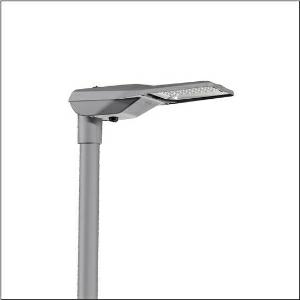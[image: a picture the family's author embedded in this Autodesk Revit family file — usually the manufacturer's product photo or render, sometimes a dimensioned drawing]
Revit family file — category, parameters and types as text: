
# Revit family: streetlight_sl_21_mini___p0_5a_5xe2v33t08gb_dcd0
name_source: partatom
category: Lighting Fixtures
units: mm (PartAtom-declared; Revit-internal decimal feet)

## family parameters
Cut with Voids When Loaded = No
Host = Face
Light Source = No
Part Type = Normal
Room Calculation Point = No
Round Connector Dimension = Use Diameter
Shared = No

## types (1)
- --- (1 x LED, 5840 lm, 40.4 W, 3000K)
    Apparent Load = 40 VA
    CIE Flux Codes = 37 73 96 100 100
    Color Rendering = 70
    Color Temperature = 3000K
    Default Elevation = 1800 mm
    Description = Streetlight SL 21 mini, mast luminaire, primary light control with lens, of PMMA, primary optical cover: cover, of toughened safety glass, transparent, light distribution: P0.5a, light emission: direct distribution, primary light characteristic: asymmetric, installation type: post-top, side-entry, LED, High Power LED, rated luminous flux: 5.840lm, luminous efficacy: 145lm/W, light colour: 730, colour temperature: 3000K, control gear: D4i, control: pre-setting: logarithmic dimming characteristic, flexible luminous flux parameterisation, time-dependent luminous flux control, constant luminous flux control, overheat protection, mains connection: 220..240V, AC, 50/60Hz, start of lifetime: 40W, end of service life: 41W, reduction: 19W, luminaire housing, of diecast aluminium, powder-coated, SITECO metallic grey (DB 702S), corrosivity category C5 high according to DIN EN ISO 12944, multi-level sealing system, sealing non-destructively replaceable, inclination adjustable: 0°, 5°, 10°, 15°, please order mast flange separately, length: 628mm, width: 235mm, height: 110mm, mast flange for spigot size: 42mm (side-entry): 5XC10008XM4, 60/48mm (side-entry/post-top): 5XC10108XM2, 76/60mm (side-entry/post-top): 5XC10108XM1, mounting height: 4..8m, Smart Interface below and above, protection rating (complete): IP66, insulation class (complete): insulation class II (safety insulation), certification: CE, ENEC, ENEC+, VDE, impact resistance: IK10, permissible operating ambient temperature for outdoor applications: -40..+50°C, standard-compliant lighting for roads and squares, packaging unit: 1 piece

Light Distribution: P0.5a
    Height = 110 mm
    Lamp = 1 x LED
    Lamp Light Flux = 5840 lm
    Lamp Power = 40.4 W
    Lamp count = 1
    Length = 625 mm
    Luminous efficacy = 145 lm/W
    Manufacturer = Siteco
    ModVariant = No
    Model = 5XE2V33T08GB
    Number of Poles = 1
    OnlyDefault = Yes
    Power Factor = 1
    Product Name = Streetlight SL 21 mini | P0.5a
    Product group = mast luminaire | pylon top
    ProductGroupID = 6100
    Protection Class = Protection class II
    Protection Degree = IP 66
    RLX_Detail_Level = 1
    RLX_Emergency_Light_Flux = 0 lm
    RLX_Emergency_Type = 0
    RLX_Emergency_Type_DB = No
    RlxData = <blob elided: 91717 chars, md5=268cba24>
    Socket = socket
    Standby Power = 0 W
    System Light Flux = 5840 lm
    System Power = 40 W
    Type Comments = factory setting: luminous flux: 100 % | dim-lin: 254 | 812 mA
    Type Image = l_1003514.jpg
    URL = http://relux.com
    VarID = @adj_077243
    Voltage = 0 V
    Weight = 0.00 kg
    Width = 234 mm

## geometry (parser evidence)
native form markers: Blend x4, Sweep x11
no freeform markers — native parametric forms only
